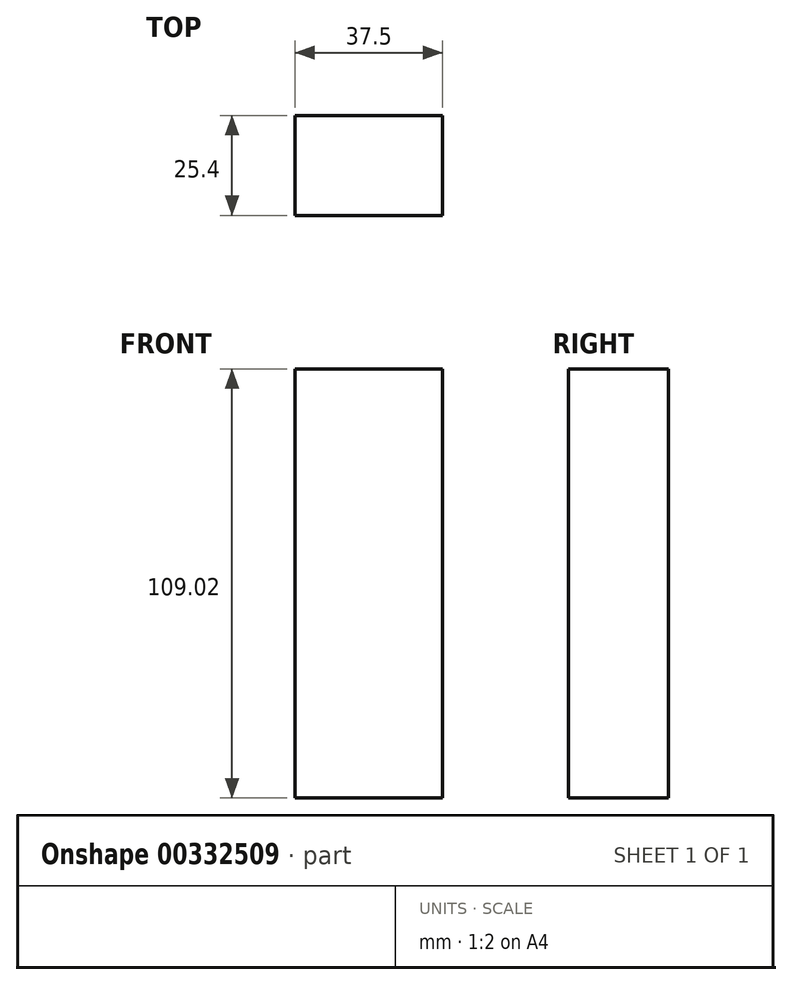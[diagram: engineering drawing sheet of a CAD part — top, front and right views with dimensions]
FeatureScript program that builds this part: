
annotation { "Feature Type Name" : "Feature", "Feature Type Description" : "" }
export const myFeature = defineFeature(function(context is Context, id is Id, definition is map)
    precondition{}
    {
        {
            var Q0;
            Q0=qCreatedBy(makeId("Front.planeOp"),FACE);
            var sketch = newSketch(context, id + "F0", { "sketchPlane" : qUnion([Q0])});
            skLineSegment(sketch, "E0.bottom", {"start": v(-37.5, 53.18) * mm, "end": v(0, 53.18) * mm});
            skLineSegment(sketch, "E0.top", {"start": v(-37.5, -55.84) * mm, "end": v(0, -55.84) * mm});
            skLineSegment(sketch, "E0.left", {"start": v(-37.5, 53.18) * mm, "end": v(-37.5, -55.84) * mm});
            skLineSegment(sketch, "E0.right", {"start": v(0, 53.18) * mm, "end": v(0, -55.84) * mm});
            skSolve(sketch);
        }
        {
            var Q0;
            Q0 = qSketchRegion(id + "F0", true);
            extrude(context, id + "F1", {"entities" : qUnion([Q0]), "depth" : 25.4 * mm});
        }
    });
